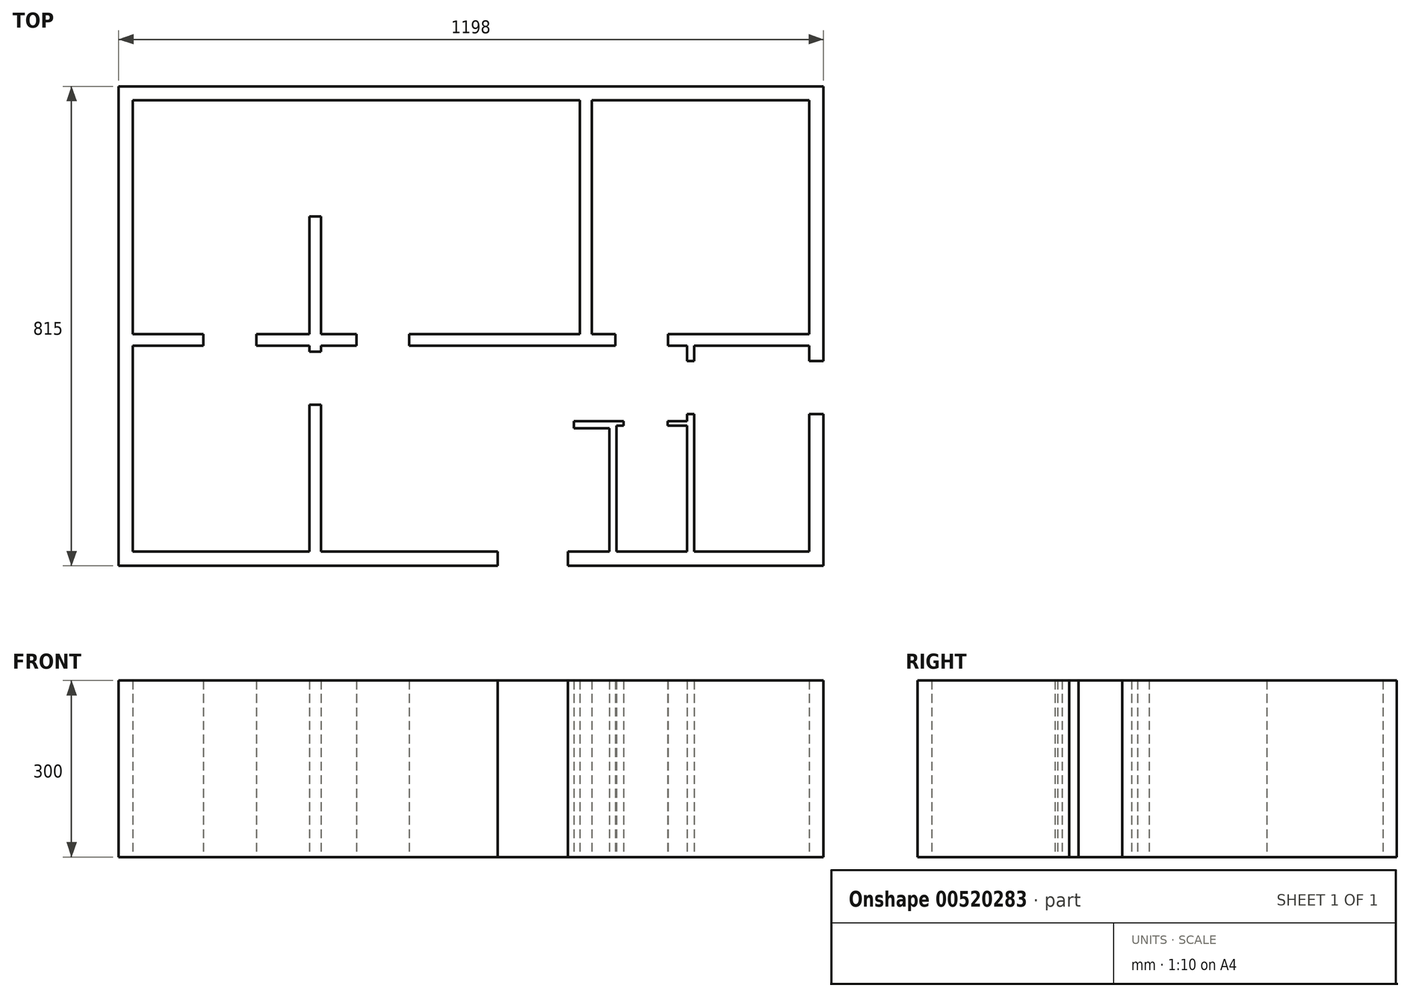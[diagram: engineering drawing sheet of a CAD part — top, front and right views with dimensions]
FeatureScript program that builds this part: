
annotation { "Feature Type Name" : "Feature", "Feature Type Description" : "" }
export const myFeature = defineFeature(function(context is Context, id is Id, definition is map)
    precondition{}
    {
        {
            var Q0;
            Q0=qCreatedBy(makeId("Top.planeOp"),FACE);
            var sketch = newSketch(context, id + "F0", { "sketchPlane" : qUnion([Q0])});
            skLineSegment(sketch, "E0.bottom", {"start": v(0, 0) * mm, "end": v(-434, 0) * mm});
            skLineSegment(sketch, "E0.top", {"start": v(0, 815) * mm, "end": v(-1198, 815) * mm});
            skLineSegment(sketch, "E0.left", {"start": v(0, 0) * mm, "end": v(0, 258) * mm});
            skLineSegment(sketch, "E0.right", {"start": v(-1198, 0) * mm, "end": v(-1198, 815) * mm});
            skLineSegment(sketch, "E1", {"start": v(-1174, 791) * mm, "end": v(-1174, 394) * mm});
            skLineSegment(sketch, "E2", {"start": v(-1174, 24) * mm, "end": v(-874, 24) * mm});
            skLineSegment(sketch, "E3", {"start": v(-24, 24) * mm, "end": v(-24, 258) * mm});
            skLineSegment(sketch, "E4", {"start": v(-24, 791) * mm, "end": v(-394, 791) * mm});
            skLineSegment(sketch, "E5", {"start": v(-1174, 374) * mm, "end": v(-1054, 374) * mm});
            skLineSegment(sketch, "E6", {"start": v(-1174, 394) * mm, "end": v(-1054, 394) * mm});
            skLineSegment(sketch, "E7", {"start": v(-874, 24) * mm, "end": v(-874, 274) * mm});
            skLineSegment(sketch, "E8", {"start": v(-874, 274) * mm, "end": v(-854, 274) * mm});
            skLineSegment(sketch, "E9", {"start": v(-854, 274) * mm, "end": v(-854, 24) * mm});
            skLineSegment(sketch, "E10", {"start": v(-1054, 394) * mm, "end": v(-1054, 374) * mm});
            skLineSegment(sketch, "E11", {"start": v(-964, 394) * mm, "end": v(-964, 374) * mm});
            skLineSegment(sketch, "E12", {"start": v(-794, 394) * mm, "end": v(-794, 374) * mm});
            skLineSegment(sketch, "E13", {"start": v(-704, 394) * mm, "end": v(-704, 374) * mm});
            skLineSegment(sketch, "E14.trimOffspring", {"start": v(-964, 394) * mm, "end": v(-874, 394) * mm});
            skLineSegment(sketch, "E15.trimOffspring", {"start": v(-704, 394) * mm, "end": v(-414, 394) * mm});
            skLineSegment(sketch, "E16.trimOffspring", {"start": v(-704, 374) * mm, "end": v(-354, 374) * mm});
            skLineSegment(sketch, "E17.trimOffspring", {"start": v(-964, 374) * mm, "end": v(-874, 374) * mm});
            skLineSegment(sketch, "E18", {"start": v(-414, 394) * mm, "end": v(-414, 791) * mm});
            skLineSegment(sketch, "E19", {"start": v(-394, 791) * mm, "end": v(-394, 394) * mm});
            skLineSegment(sketch, "E20.trimOffspring", {"start": v(-394, 394) * mm, "end": v(-354, 394) * mm});
            skLineSegment(sketch, "E21", {"start": v(-354, 394) * mm, "end": v(-354, 374) * mm});
            skLineSegment(sketch, "E22", {"start": v(-264, 394) * mm, "end": v(-264, 374) * mm});
            skLineSegment(sketch, "E23.trimOffspring", {"start": v(-264, 394) * mm, "end": v(-24, 394) * mm});
            skLineSegment(sketch, "E24.trimOffspring", {"start": v(-264, 374) * mm, "end": v(-232, 374) * mm});
            skLineSegment(sketch, "E25.trimOffspring", {"start": v(-854, 24) * mm, "end": v(-554, 24) * mm});
            skLineSegment(sketch, "E26.trimOffspring", {"start": v(-24, 394) * mm, "end": v(-24, 791) * mm});
            skLineSegment(sketch, "E27.trimOffspring", {"start": v(-1174, 374) * mm, "end": v(-1174, 24) * mm});
            skLineSegment(sketch, "E28", {"start": v(-874, 374) * mm, "end": v(-874, 364) * mm});
            skLineSegment(sketch, "E29", {"start": v(-874, 364) * mm, "end": v(-854, 364) * mm});
            skLineSegment(sketch, "E30", {"start": v(-854, 364) * mm, "end": v(-854, 374) * mm});
            skLineSegment(sketch, "E31.trimOffspring", {"start": v(-854, 374) * mm, "end": v(-794, 374) * mm});
            skLineSegment(sketch, "E32.trimOffspring", {"start": v(-414, 791) * mm, "end": v(-1174, 791) * mm});
            skLineSegment(sketch, "E33", {"start": v(-554, 24) * mm, "end": v(-554, 0) * mm});
            skLineSegment(sketch, "E34", {"start": v(-434, 24) * mm, "end": v(-434, 0) * mm});
            skLineSegment(sketch, "E35.trimOffspring", {"start": v(-434, 24) * mm, "end": v(-24, 24) * mm});
            skLineSegment(sketch, "E36.trimOffspring", {"start": v(-554, 0) * mm, "end": v(-1198, 0) * mm});
            skLineSegment(sketch, "E37", {"start": v(-364, 24) * mm, "end": v(-364, 234) * mm});
            skLineSegment(sketch, "E38", {"start": v(-364, 234) * mm, "end": v(-424, 234) * mm});
            skLineSegment(sketch, "E39", {"start": v(-424, 234) * mm, "end": v(-424, 246) * mm});
            skLineSegment(sketch, "E40", {"start": v(-424, 246) * mm, "end": v(-340, 246) * mm});
            skLineSegment(sketch, "E41", {"start": v(-340, 246) * mm, "end": v(-340, 238) * mm});
            skLineSegment(sketch, "E42", {"start": v(-340, 238) * mm, "end": v(-352, 238) * mm});
            skLineSegment(sketch, "E43", {"start": v(-352, 238) * mm, "end": v(-352, 24) * mm});
            skLineSegment(sketch, "E44", {"start": v(-265, 246) * mm, "end": v(-232, 246) * mm});
            skLineSegment(sketch, "E45", {"start": v(-232, 246) * mm, "end": v(-232, 258) * mm});
            skLineSegment(sketch, "E46", {"start": v(-232, 258) * mm, "end": v(-220, 258) * mm});
            skLineSegment(sketch, "E47", {"start": v(-220, 258) * mm, "end": v(-220, 24) * mm});
            skLineSegment(sketch, "E48", {"start": v(-265, 246) * mm, "end": v(-265, 238) * mm});
            skLineSegment(sketch, "E49", {"start": v(-265, 238) * mm, "end": v(-232, 238) * mm});
            skLineSegment(sketch, "E50", {"start": v(-232, 238) * mm, "end": v(-232, 24) * mm});
            skLineSegment(sketch, "E51", {"start": v(-874, 394) * mm, "end": v(-874, 594) * mm});
            skLineSegment(sketch, "E52", {"start": v(-874, 594) * mm, "end": v(-854, 594) * mm});
            skLineSegment(sketch, "E53", {"start": v(-854, 594) * mm, "end": v(-854, 394) * mm});
            skLineSegment(sketch, "E54.trimOffspring", {"start": v(-854, 394) * mm, "end": v(-794, 394) * mm});
            skLineSegment(sketch, "E55", {"start": v(-232, 374) * mm, "end": v(-232, 348) * mm});
            skLineSegment(sketch, "E56", {"start": v(-232, 348) * mm, "end": v(-220, 348) * mm});
            skLineSegment(sketch, "E57", {"start": v(-220, 348) * mm, "end": v(-220, 374) * mm});
            skLineSegment(sketch, "E58.trimOffspring", {"start": v(-220, 374) * mm, "end": v(-24, 374) * mm});
            skLineSegment(sketch, "E59", {"start": v(-24, 348) * mm, "end": v(0, 348) * mm});
            skLineSegment(sketch, "E60", {"start": v(-24, 258) * mm, "end": v(0, 258) * mm});
            skLineSegment(sketch, "E61.trimOffspring", {"start": v(-24, 348) * mm, "end": v(-24, 374) * mm});
            skLineSegment(sketch, "E62.trimOffspring", {"start": v(0, 348) * mm, "end": v(0, 815) * mm});
            skSolve(sketch);
        }
        {
            var Q0;
            Q0 = qSketchRegion(id + "F0", true);
            extrude(context, id + "F1", {"entities" : qUnion([Q0]), "depth" : 300 * mm, "offsetDistance" : 25 * mm});
        }
    });
